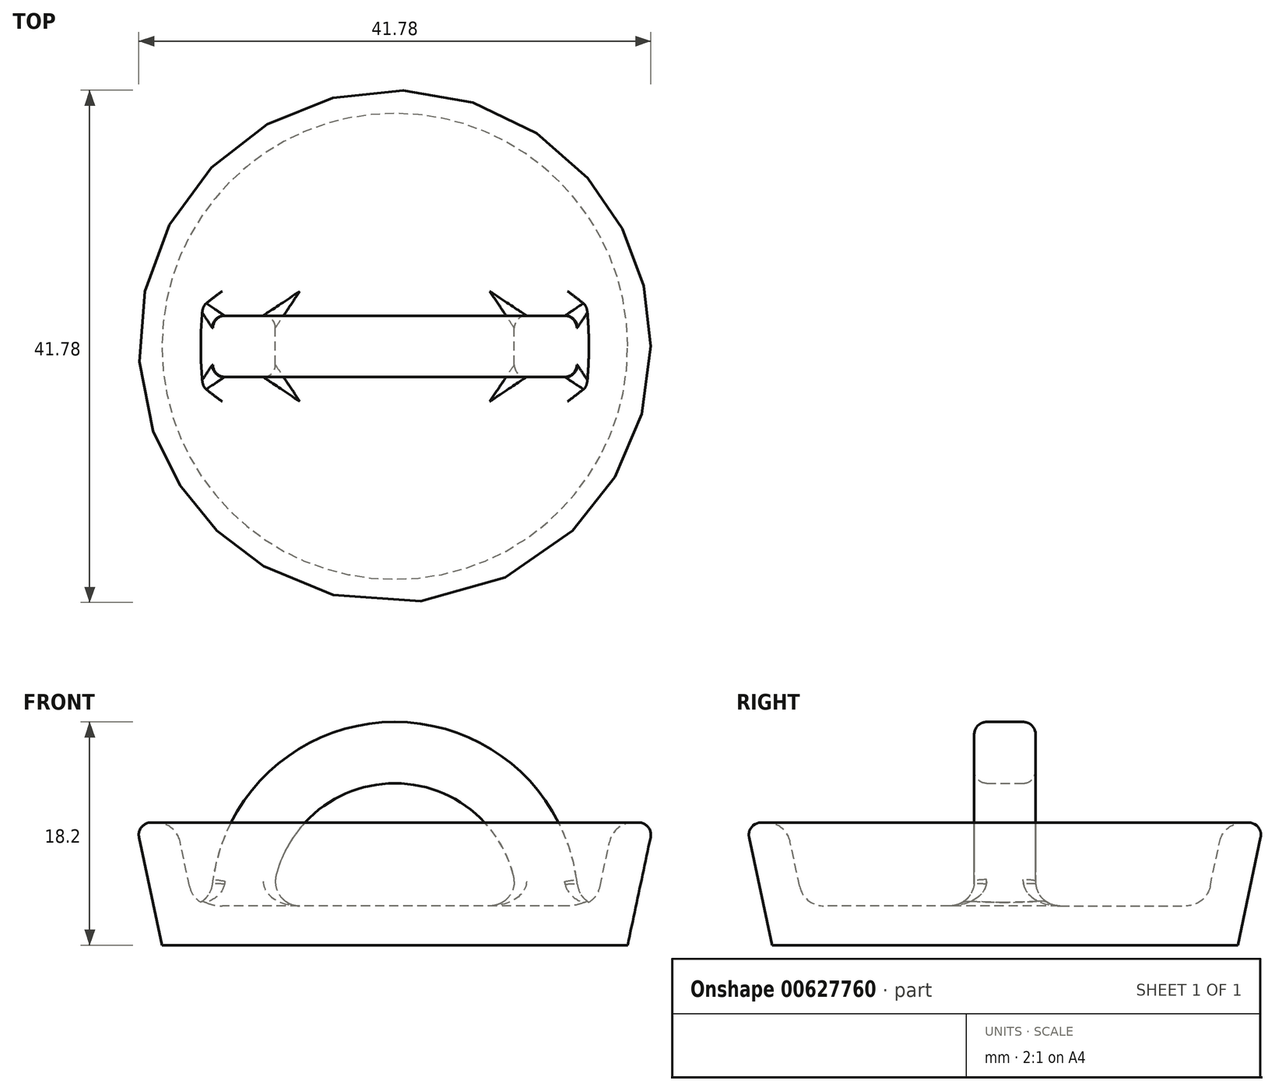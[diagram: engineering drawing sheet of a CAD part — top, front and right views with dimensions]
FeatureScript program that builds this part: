
annotation { "Feature Type Name" : "Feature", "Feature Type Description" : "" }
export const myFeature = defineFeature(function(context is Context, id is Id, definition is map)
    precondition{}
    {
        {
            var Q0;
            Q0=qCreatedBy(makeId("Top.planeOp"),FACE);
            var sketch = newSketch(context, id + "F0", { "sketchPlane" : qUnion([Q0])});
            skCircle(sketch, "E0", {"center": v(0, 0) * mm, "radius": 19 * mm});
            skSolve(sketch);
        }
        {
            var Q0;
            Q0=makeQuery(id+"F0.imprint","IMPRINT",FACE,{"disambiguationData":[TD([[makeQuery(id+"F0.imprint","IMPRINT",EDGE,{"derivedFrom":sQuery(id+"F0.wireOp",EDGE,"E0")}),1.0]])]});
            extrude(context, id + "F1", {"entities" : qUnion([Q0]), "depth" : 10 * mm, "offsetDistance" : 25 * mm, "hasDraft" : true, "draftAngle" : 12 * degree});
        }
        {
            var Q0;
            Q0=makeQuery(id+"F1.opExtrude","CAP_FACE",FACE,{"disambiguationData":[OSD([sQuery(id+"F0.wireOp",EDGE,"E0")])],"isStart":false});
            shell(context, id + "F2", {"entities" : qUnion([Q0]), "thickness" : (1.6 * 2) * mm});
        }
        {
            var Q0;
            Q0=qCreatedBy(makeId("Front.planeOp"),FACE);
            var sketch = newSketch(context, id + "F3", { "sketchPlane" : qUnion([Q0])});
            skLineSegment(sketch, "E1.0.0", {"start": v(-16.4, 3.2) * mm, "end": v(16.4, 3.2) * mm, "construction": true});
            skArc(sketch, "E2", {"start": v(15, 3.2) * mm, "mid": v(0, 18.2) * mm, "end": v(-15, 3.2) * mm});
            skArc(sketch, "E3.0", {"start": v(10, 3.2) * mm, "mid": v(0, 13.2) * mm, "end": v(-10, 3.2) * mm});
            skLineSegment(sketch, "E4", {"start": v(15, 3.2) * mm, "end": v(10, 3.2) * mm});
            skLineSegment(sketch, "E5", {"start": v(-10, 3.2) * mm, "end": v(-15, 3.2) * mm});
            skSolve(sketch);
        }
        {
            var Q0;
            Q0=makeQuery(id+"F3.imprint","IMPRINT",FACE,{"disambiguationData":[TD([[makeQuery(id+"F3.imprint","IMPRINT",EDGE,{"derivedFrom":sQuery(id+"F3.wireOp",EDGE,"E2")}),1.0]])]});
            extrude(context, id + "F4", {"entities" : qUnion([Q0]), "operationType" : NewBodyOperationType.ADD, "endBound" : BoundingType.SYMMETRIC, "depth" : 5 * mm, "offsetDistance" : 25 * mm});
        }
        {
            var Q0;
            {var subQ0=sQuery(id+"F0.wireOp",EDGE,"E0");Q0=makeQuery(id+"F2.opShell","OFFSET_EDGE",EDGE,{"disambiguationData":[OSD([subQ0]),TDD([makeQuery(id+"F1.opExtrude","CAP_EDGE",EDGE,{"disambiguationData":[OSD([subQ0])],"isStart":true})])]});}
            var Q1;
            Q1=makeQuery(id+"F4.opExtrude","CAP_EDGE",EDGE,{"disambiguationData":[OSD([sQuery(id+"F3.wireOp",EDGE,"E5")])],"isStart":true});
            var Q2;
            Q2=makeQuery(id+"F4.opExtrude","SWEPT_EDGE",EDGE,{"disambiguationData":[OSD([sQuery(id+"F3.wireOp",EDGE,"E3.0"),sQuery(id+"F3.wireOp",EDGE,"E5")])]});
            var Q3;
            Q3=makeQuery(id+"F4.opExtrude","CAP_EDGE",EDGE,{"disambiguationData":[OSD([sQuery(id+"F3.wireOp",EDGE,"E5")])],"isStart":false});
            var Q4;
            {var subQ0=sQuery(id+"F0.wireOp",EDGE,"E0");Q4=makeQuery(id+"F2.opShell","OFFSET_FACE",FACE,{"disambiguationData":[OSD([subQ0]),TDD([makeQuery(id+"F1.opExtrude","CAP_FACE",FACE,{"disambiguationData":[OSD([subQ0])],"isStart":true})])]});}
            var Q5;
            {var subQ0=sQuery(id+"F0.wireOp",EDGE,"E0");Q5=makeQuery(id+"F2.opShell","OFFSET_EDGE",EDGE,{"disambiguationData":[OSD([subQ0]),TDD([makeQuery(id+"F1.opExtrude","CAP_EDGE",EDGE,{"disambiguationData":[OSD([subQ0])],"isStart":false})])]});}
            fillet(context, id + "F5", {"entities" : qUnion([Q0, Q1, Q2, Q3, Q4, Q5]), "radius" : 2 * mm, "tangentPropagation" : true, "allowEdgeOverflow" : false});
        }
        {
            var Q0;
            Q0=makeQuery(id+"F4.opExtrude","CAP_EDGE",EDGE,{"disambiguationData":[OSD([sQuery(id+"F3.wireOp",EDGE,"E2")])],"isStart":false});
            var Q1;
            Q1=makeQuery(id+"F4.opExtrude","CAP_EDGE",EDGE,{"disambiguationData":[OSD([sQuery(id+"F3.wireOp",EDGE,"E2")])],"isStart":true});
            var Q2;
            Q2=makeQuery(id+"F4.opExtrude","CAP_EDGE",EDGE,{"disambiguationData":[OSD([sQuery(id+"F3.wireOp",EDGE,"E3.0")])],"isStart":false});
            var Q3;
            Q3=makeQuery(id+"F4.opExtrude","CAP_EDGE",EDGE,{"disambiguationData":[OSD([sQuery(id+"F3.wireOp",EDGE,"E3.0")])],"isStart":true});
            var Q4;
            Q4=makeQuery(id+"F1.opExtrude","CAP_EDGE",EDGE,{"disambiguationData":[OSD([sQuery(id+"F0.wireOp",EDGE,"E0")])],"isStart":false});
            fillet(context, id + "F6", {"entities" : qUnion([Q0, Q1, Q2, Q3, Q4]), "radius" : 1 * mm, "tangentPropagation" : true, "allowEdgeOverflow" : false});
        }
    });
